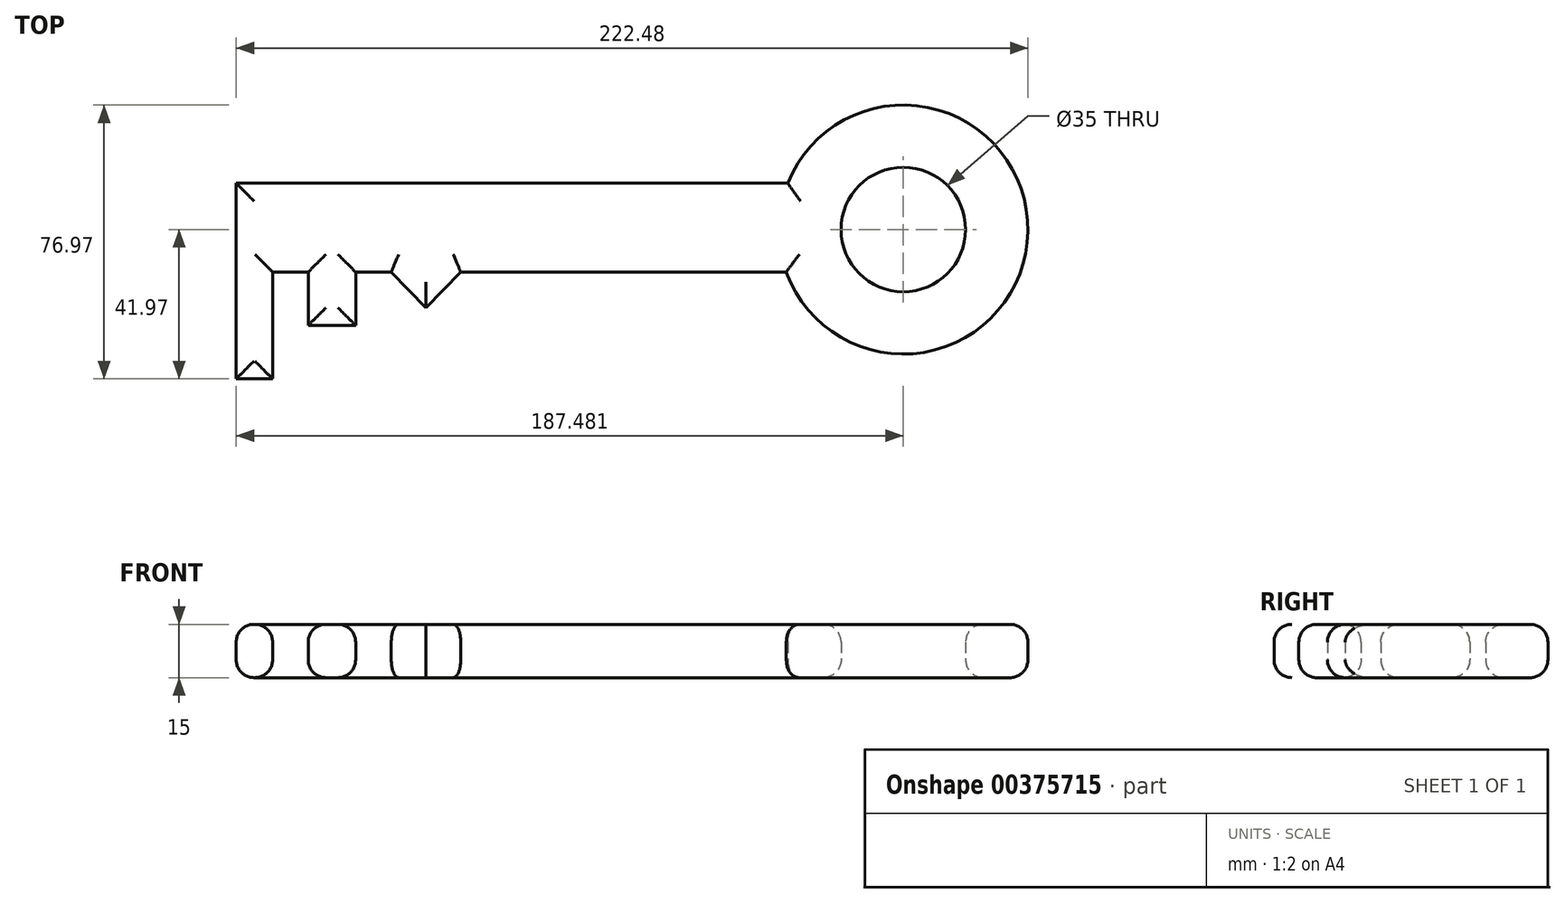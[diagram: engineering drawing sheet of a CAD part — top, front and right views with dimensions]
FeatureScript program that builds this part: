
annotation { "Feature Type Name" : "Feature", "Feature Type Description" : "" }
export const myFeature = defineFeature(function(context is Context, id is Id, definition is map)
    precondition{}
    {
        {
            var Q0;
            Q0=qCreatedBy(makeId("Top.planeOp"),FACE);
            var sketch = newSketch(context, id + "F0", { "sketchPlane" : qUnion([Q0])});
            skLineSegment(sketch, "E0.bottom", {"start": v(-107.05, 25) * mm, "end": v(47.95, 25) * mm});
            skLineSegment(sketch, "E0.top", {"start": v(-96.8, 0) * mm, "end": v(-86.8, 0) * mm});
            skLineSegment(sketch, "E0.left", {"start": v(-107.05, 25) * mm, "end": v(-107.05, 0) * mm});
            skLineSegment(sketch, "E1.top", {"start": v(-107.05, -30) * mm, "end": v(-96.8, -30) * mm});
            skLineSegment(sketch, "E1.left", {"start": v(-107.05, 0) * mm, "end": v(-107.05, -30) * mm});
            skLineSegment(sketch, "E1.right", {"start": v(-96.8, 0) * mm, "end": v(-96.8, -30) * mm});
            skLineSegment(sketch, "E2.top", {"start": v(-86.8, -15) * mm, "end": v(-73.47, -15) * mm});
            skLineSegment(sketch, "E2.left", {"start": v(-86.8, 0) * mm, "end": v(-86.8, -15) * mm});
            skLineSegment(sketch, "E2.right", {"start": v(-73.47, 0) * mm, "end": v(-73.47, -15) * mm});
            skLineSegment(sketch, "E3", {"start": v(-63.47, 0) * mm, "end": v(-53.68, -10) * mm});
            skArc(sketch, "E4", {"start": v(47.54, 0) * mm, "mid": v(115.43, 11.4) * mm, "end": v(47.95, 25) * mm});
            skLineSegment(sketch, "E5", {"start": v(-53.68, -10) * mm, "end": v(-43.95, 0) * mm});
            skCircle(sketch, "E6", {"center": v(80.43, 11.97) * mm, "radius": 17.5 * mm});
            skLineSegment(sketch, "E7.trimOffspring", {"start": v(-73.47, 0) * mm, "end": v(-63.47, 0) * mm});
            skLineSegment(sketch, "E8.trimOffspring", {"start": v(-43.95, 0) * mm, "end": v(47.54, 0) * mm});
            skSolve(sketch);
        }
        {
            var Q0;
            Q0=makeQuery(id+"F0.imprint","IMPRINT",FACE,{"disambiguationData":[TD([[makeQuery(id+"F0.imprint","IMPRINT",EDGE,{"derivedFrom":sQuery(id+"F0.wireOp",EDGE,"E0.bottom")}),-1.0]])]});
            extrude(context, id + "F1", {"entities" : qUnion([Q0]), "depth" : 15 * mm});
        }
        {
            var Q0;
            Q0=makeQuery(id+"F1.opExtrude","CAP_EDGE",EDGE,{"disambiguationData":[OSD([sQuery(id+"F0.wireOp",EDGE,"E0.bottom")])],"isStart":false});
            var Q1;
            Q1=makeQuery(id+"F1.opExtrude","CAP_EDGE",EDGE,{"disambiguationData":[OSD([sQuery(id+"F0.wireOp",EDGE,"E0.left"),sQuery(id+"F0.wireOp",EDGE,"E1.left")])],"isStart":false});
            var Q2;
            Q2=makeQuery(id+"F1.opExtrude","CAP_EDGE",EDGE,{"disambiguationData":[OSD([sQuery(id+"F0.wireOp",EDGE,"E1.right")])],"isStart":false});
            var Q3;
            Q3=makeQuery(id+"F1.opExtrude","CAP_EDGE",EDGE,{"disambiguationData":[OSD([sQuery(id+"F0.wireOp",EDGE,"E1.top")])],"isStart":false});
            var Q4;
            Q4=makeQuery(id+"F1.opExtrude","CAP_EDGE",EDGE,{"disambiguationData":[OSD([sQuery(id+"F0.wireOp",EDGE,"E2.left")])],"isStart":false});
            var Q5;
            Q5=makeQuery(id+"F1.opExtrude","CAP_EDGE",EDGE,{"disambiguationData":[OSD([sQuery(id+"F0.wireOp",EDGE,"E2.top")])],"isStart":false});
            var Q6;
            Q6=makeQuery(id+"F1.opExtrude","CAP_EDGE",EDGE,{"disambiguationData":[OSD([sQuery(id+"F0.wireOp",EDGE,"E2.right")])],"isStart":false});
            var Q7;
            Q7=makeQuery(id+"F1.opExtrude","CAP_EDGE",EDGE,{"disambiguationData":[OSD([sQuery(id+"F0.wireOp",EDGE,"E7.trimOffspring")])],"isStart":false});
            var Q8;
            Q8=makeQuery(id+"F1.opExtrude","CAP_EDGE",EDGE,{"disambiguationData":[OSD([sQuery(id+"F0.wireOp",EDGE,"E0.top")])],"isStart":false});
            var Q9;
            Q9=makeQuery(id+"F1.opExtrude","CAP_EDGE",EDGE,{"disambiguationData":[OSD([sQuery(id+"F0.wireOp",EDGE,"E3")])],"isStart":false});
            var Q10;
            Q10=makeQuery(id+"F1.opExtrude","CAP_EDGE",EDGE,{"disambiguationData":[OSD([sQuery(id+"F0.wireOp",EDGE,"E5")])],"isStart":false});
            var Q11;
            Q11=makeQuery(id+"F1.opExtrude","CAP_EDGE",EDGE,{"disambiguationData":[OSD([sQuery(id+"F0.wireOp",EDGE,"E8.trimOffspring")])],"isStart":false});
            var Q12;
            Q12=makeQuery(id+"F1.opExtrude","CAP_EDGE",EDGE,{"disambiguationData":[OSD([sQuery(id+"F0.wireOp",EDGE,"E4")])],"isStart":false});
            var Q13;
            Q13=makeQuery(id+"F1.opExtrude","CAP_EDGE",EDGE,{"disambiguationData":[OSD([sQuery(id+"F0.wireOp",EDGE,"E6")])],"isStart":false});
            fillet(context, id + "F2", {"entities" : qUnion([Q0, Q1, Q2, Q3, Q4, Q5, Q6, Q7, Q8, Q9, Q10, Q11, Q12, Q13]), "radius" : 5 * mm, "tangentPropagation" : true, "allowEdgeOverflow" : false});
        }
        {
            var Q0;
            Q0=makeQuery(id+"F1.opExtrude","CAP_EDGE",EDGE,{"disambiguationData":[OSD([sQuery(id+"F0.wireOp",EDGE,"E4")])],"isStart":true});
            var Q1;
            Q1=makeQuery(id+"F1.opExtrude","CAP_EDGE",EDGE,{"disambiguationData":[OSD([sQuery(id+"F0.wireOp",EDGE,"E8.trimOffspring")])],"isStart":true});
            var Q2;
            Q2=makeQuery(id+"F1.opExtrude","CAP_EDGE",EDGE,{"disambiguationData":[OSD([sQuery(id+"F0.wireOp",EDGE,"E5")])],"isStart":true});
            var Q3;
            Q3=makeQuery(id+"F1.opExtrude","CAP_EDGE",EDGE,{"disambiguationData":[OSD([sQuery(id+"F0.wireOp",EDGE,"E3")])],"isStart":true});
            var Q4;
            Q4=makeQuery(id+"F1.opExtrude","CAP_EDGE",EDGE,{"disambiguationData":[OSD([sQuery(id+"F0.wireOp",EDGE,"E7.trimOffspring")])],"isStart":true});
            var Q5;
            Q5=makeQuery(id+"F1.opExtrude","CAP_EDGE",EDGE,{"disambiguationData":[OSD([sQuery(id+"F0.wireOp",EDGE,"E2.right")])],"isStart":true});
            var Q6;
            Q6=makeQuery(id+"F1.opExtrude","CAP_EDGE",EDGE,{"disambiguationData":[OSD([sQuery(id+"F0.wireOp",EDGE,"E2.top")])],"isStart":true});
            var Q7;
            Q7=makeQuery(id+"F1.opExtrude","CAP_EDGE",EDGE,{"disambiguationData":[OSD([sQuery(id+"F0.wireOp",EDGE,"E0.top")])],"isStart":true});
            var Q8;
            Q8=makeQuery(id+"F1.opExtrude","CAP_FACE",FACE,{"disambiguationData":[OSD([sQuery(id+"F0.wireOp",EDGE,"E0.bottom"),sQuery(id+"F0.wireOp",EDGE,"E0.top"),sQuery(id+"F0.wireOp",EDGE,"E0.left"),sQuery(id+"F0.wireOp",EDGE,"E1.top"),sQuery(id+"F0.wireOp",EDGE,"E1.left"),sQuery(id+"F0.wireOp",EDGE,"E1.right"),sQuery(id+"F0.wireOp",EDGE,"E2.top"),sQuery(id+"F0.wireOp",EDGE,"E2.left"),sQuery(id+"F0.wireOp",EDGE,"E2.right"),sQuery(id+"F0.wireOp",EDGE,"E3"),sQuery(id+"F0.wireOp",EDGE,"E4"),sQuery(id+"F0.wireOp",EDGE,"E5"),sQuery(id+"F0.wireOp",EDGE,"E6"),sQuery(id+"F0.wireOp",EDGE,"E7.trimOffspring"),sQuery(id+"F0.wireOp",EDGE,"E8.trimOffspring")])],"isStart":true});
            fillet(context, id + "F3", {"entities" : qUnion([Q0, Q1, Q2, Q3, Q4, Q5, Q6, Q7, Q8]), "radius" : 5 * mm, "tangentPropagation" : true, "allowEdgeOverflow" : false});
        }
    });
